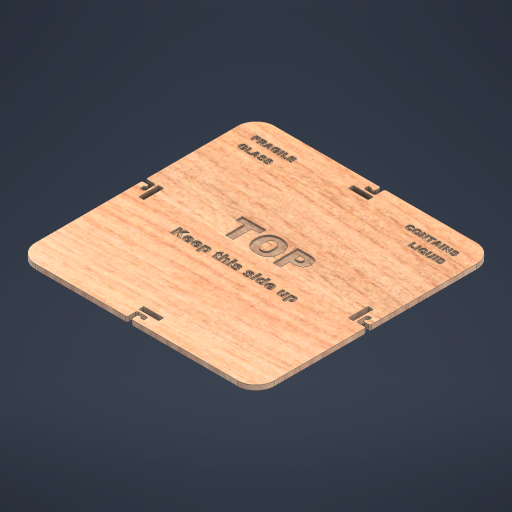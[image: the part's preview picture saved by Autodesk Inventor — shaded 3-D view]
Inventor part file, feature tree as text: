
AUTODESK INVENTOR PART (.ipt)
format: ipt  version: 2024.1 (Build 281209000, 209)  size: 1,474,048 bytes
history: native  units: mm
features: extrude x3, sketch x3, fillet x1
ambient origin geometry x8: Origin, YZ Plane, XZ Plane, XY Plane, X Axis, Y Axis, Z Axis, Center Point
bodies: Solid1 (feature_tree)
feature tree (7):
  extrude  "Extrusion1"  Depth=6.0mm
  fillet  "Fillet1"  Radius=3.0mm
  extrude  "Extrusion2"  Depth=3.0mm
  extrude  "Extrusion3"  Depth=40.0mm TaperAngle=360.0deg
  sketch  "Sketch1"  dims[d16=15.0mm d17=6.0mm d18=3.0mm]
  sketch  "Sketch2"  dims[d19=6.0mm d20=3.0mm]
  sketch  "Sketch3"  dims[d21=1.5mm d22=40.0mm d24=360.0deg d26=4.0mm d27=0.0mm d28=1.5mm d29=4.0mm d30=16.0mm d31=83.0mm d32=2.0mm d33=194.0mm d34=194.0mm d35=40.0mm d37=360.0deg d39=15.0mm d40=130.0mm d41=75.0mm d42=30.0mm d43=5.0mm d44=1.0mm d45=0.0mm d46=45.0mm d47=20.0mm d48=40.0mm d49=20.0mm d50=1.0mm d51=0.0mm]
